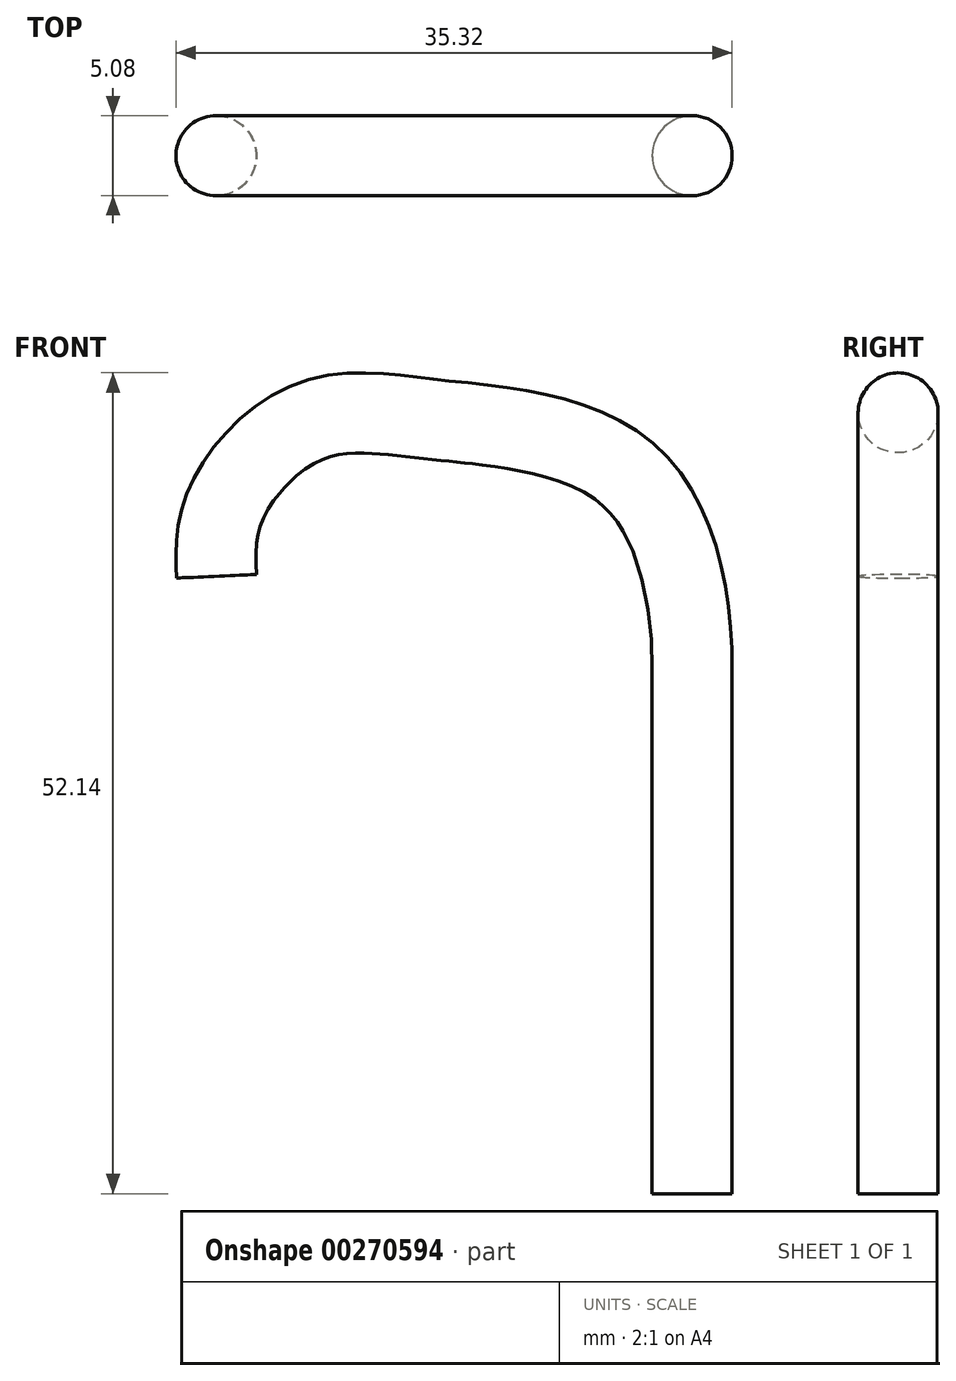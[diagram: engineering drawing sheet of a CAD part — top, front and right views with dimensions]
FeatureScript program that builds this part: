
annotation { "Feature Type Name" : "Feature", "Feature Type Description" : "" }
export const myFeature = defineFeature(function(context is Context, id is Id, definition is map)
    precondition{}
    {
        {
            var Q0;
            Q0=qCreatedBy(makeId("Top.planeOp"),FACE);
            var sketch = newSketch(context, id + "F0", { "sketchPlane" : qUnion([Q0])});
            skCircle(sketch, "E0", {"center": v(0, 0) * mm, "radius": 2.54 * mm});
            skSolve(sketch);
        }
        {
            var Q0;
            Q0=qCreatedBy(makeId("Front.planeOp"),FACE);
            var sketch = newSketch(context, id + "F1", { "sketchPlane" : qUnion([Q0])});
            skLineSegment(sketch, "E1", {"start": v(0, 0) * mm, "end": v(0, 33.28) * mm});
            skFitSpline(sketch, "E2", {"points": [v(0, 33.28) * mm, v(-3.84, 45.48) * mm, v(-15.7, 49.1) * mm], "startDerivative": vector(0, 28.68) * mm, "endDerivative": vector(-27.98, 2.75) * mm});
            skFitSpline(sketch, "E3", {"points": [v(-15.7, 49.1) * mm, v(-24.16, 49.1) * mm, v(-29.66, 43.72) * mm, v(-30.2, 39.22) * mm], "startDerivative": vector(-23.9, 2.35) * mm, "endDerivative": vector(0.71, -15.97) * mm});
            skSolve(sketch);
        }
        {
            var Q0;
            Q0=makeQuery(id+"F0.imprint","IMPRINT",FACE,{"disambiguationData":[TD([[makeQuery(id+"F0.imprint","IMPRINT",EDGE,{"derivedFrom":sQuery(id+"F0.wireOp",EDGE,"E0")}),1.0]])]});
            var Q1;
            Q1=sQuery(id+"F1.wireOp",EDGE,"E1");
            var Q2;
            Q2=sQuery(id+"F1.wireOp",EDGE,"E2");
            var Q3;
            Q3=sQuery(id+"F1.wireOp",EDGE,"617fa486-28ec-4965-8775-3eb282033897");
            var Q4;
            Q4=sQuery(id+"F1.wireOp",EDGE,"cdbdf44a-a621-4b50-a02e-60d70fac0a29");
            var Q5;
            Q5=sQuery(id+"F1.wireOp",EDGE,"E3");
            sweep(context, id + "F2", {"profiles" : qUnion([Q0]), "path" : qUnion([Q1, Q2, Q3, Q4, Q5])});
        }
    });
